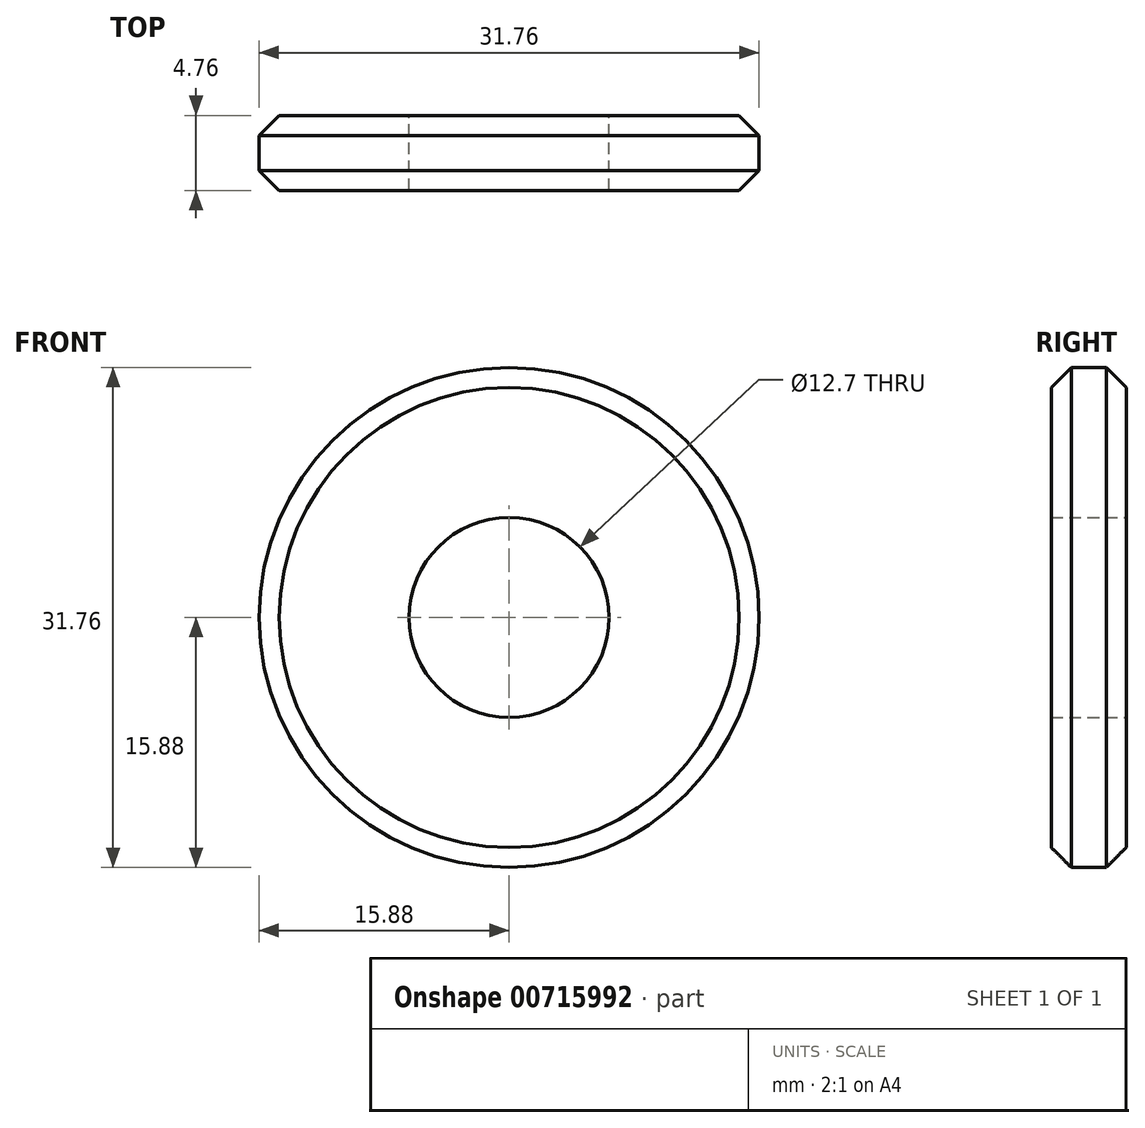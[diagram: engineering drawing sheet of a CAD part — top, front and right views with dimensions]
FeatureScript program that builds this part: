
annotation { "Feature Type Name" : "Feature", "Feature Type Description" : "" }
export const myFeature = defineFeature(function(context is Context, id is Id, definition is map)
    precondition{}
    {
        {
            var Q0;
            Q0=qCreatedBy(makeId("Front.planeOp"),FACE);
            var sketch = newSketch(context, id + "F0", { "sketchPlane" : qUnion([Q0])});
            skCircle(sketch, "E0", {"center": v(0, 0) * mm, "radius": 6.35 * mm});
            skCircle(sketch, "E1", {"center": v(0, 0) * mm, "radius": 15.88 * mm});
            skSolve(sketch);
        }
        {
            var Q0;
            Q0 = qSketchRegion(id + "F0", true);
            var Q1;
            Q1=makeQuery(id+"F0.imprint","IMPRINT",FACE,{"disambiguationData":[TD([[makeQuery(id+"F0.imprint","IMPRINT",EDGE,{"derivedFrom":sQuery(id+"F0.wireOp",EDGE,"E0")}),-1.0]])]});
            extrude(context, id + "F1", {"entities" : qUnion([Q0, Q1]), "depth" : 4.76 * mm, "offsetDistance" : 25.4 * mm});
        }
        {
            var Q0;
            Q0=makeQuery(id+"F1.opExtrude","CAP_EDGE",EDGE,{"disambiguationData":[OSD([sQuery(id+"F0.wireOp",EDGE,"E1")])],"isStart":false});
            var Q1;
            Q1=makeQuery(id+"F1.opExtrude","CAP_EDGE",EDGE,{"disambiguationData":[OSD([sQuery(id+"F0.wireOp",EDGE,"E1")])],"isStart":true});
            chamfer(context, id + "F2", {"entities" : qUnion([Q0, Q1]), "width" : 1.27 * mm, "tangentPropagation" : true});
        }
    });
